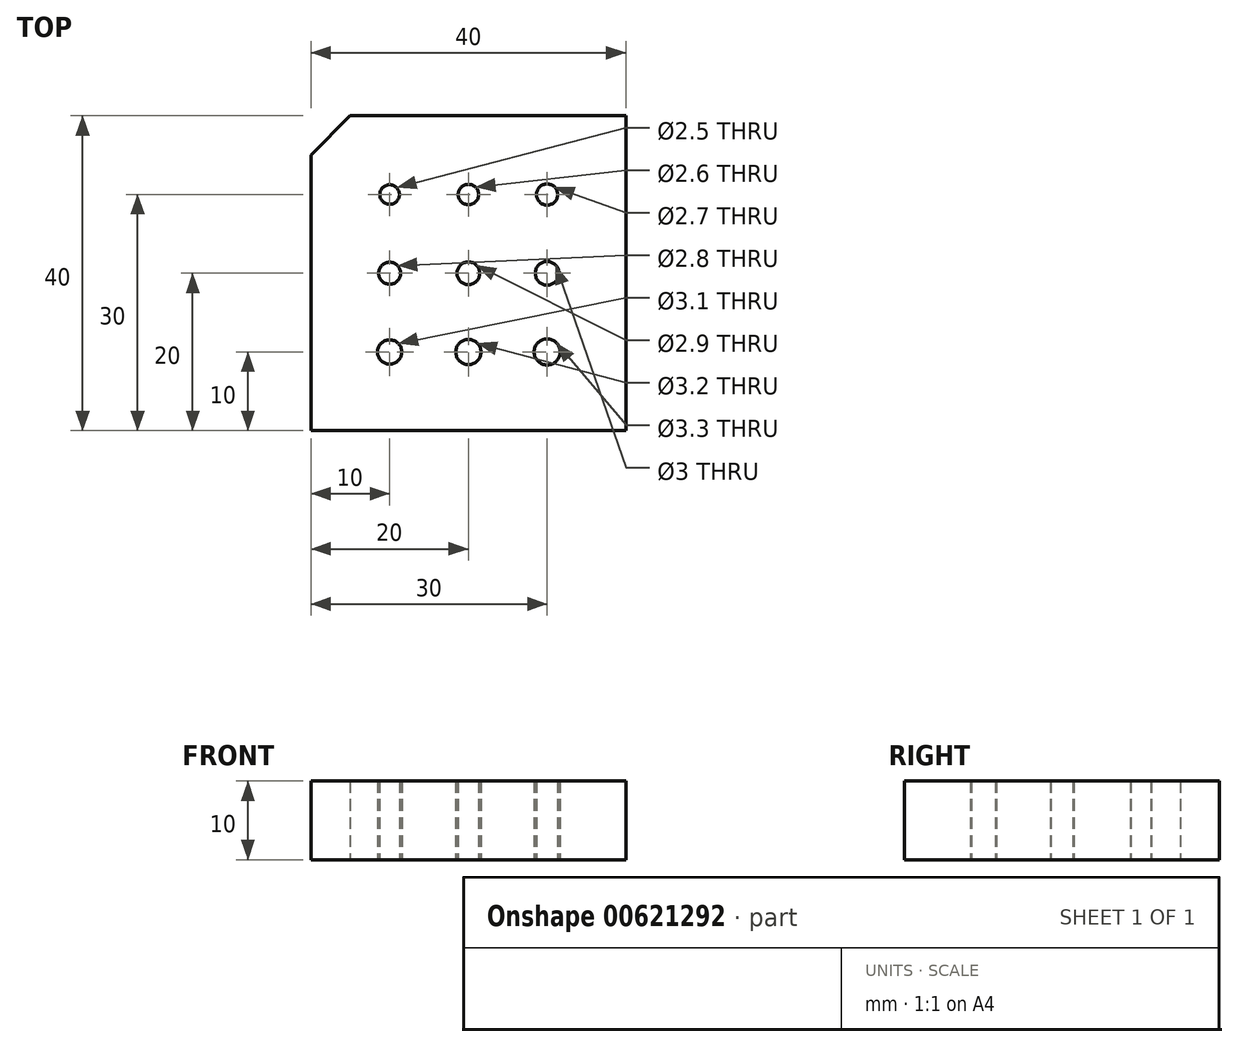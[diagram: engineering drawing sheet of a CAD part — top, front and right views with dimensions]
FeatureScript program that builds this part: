
annotation { "Feature Type Name" : "Feature", "Feature Type Description" : "" }
export const myFeature = defineFeature(function(context is Context, id is Id, definition is map)
    precondition{}
    {
        {
            var Q0;
            Q0=qCreatedBy(makeId("Top.planeOp"),FACE);
            var sketch = newSketch(context, id + "F0", { "sketchPlane" : qUnion([Q0])});
            skLineSegment(sketch, "E0.bottom", {"start": v(0, 0) * mm, "end": v(10, 0) * mm, "construction": true});
            skLineSegment(sketch, "E0.top", {"start": v(0, 10) * mm, "end": v(10, 10) * mm, "construction": true});
            skLineSegment(sketch, "E0.left", {"start": v(0, 0) * mm, "end": v(0, 10) * mm, "construction": true});
            skLineSegment(sketch, "E0.right", {"start": v(10, 0) * mm, "end": v(10, 10) * mm, "construction": true});
            skLineSegment(sketch, "E1.bottom", {"start": v(10, 0) * mm, "end": v(20, 0) * mm, "construction": true});
            skLineSegment(sketch, "E1.top", {"start": v(10, 10) * mm, "end": v(20, 10) * mm, "construction": true});
            skLineSegment(sketch, "E1.right", {"start": v(20, 0) * mm, "end": v(20, 10) * mm, "construction": true});
            skLineSegment(sketch, "E2.bottom", {"start": v(0, 0) * mm, "end": v(-10, 0) * mm, "construction": true});
            skLineSegment(sketch, "E2.top", {"start": v(0, 10) * mm, "end": v(-10, 10) * mm, "construction": true});
            skLineSegment(sketch, "E2.right", {"start": v(-10, 0) * mm, "end": v(-10, 10) * mm, "construction": true});
            skLineSegment(sketch, "E3.bottom", {"start": v(-10, 0) * mm, "end": v(-20, 0) * mm, "construction": true});
            skLineSegment(sketch, "E3.top", {"start": v(-10, 10) * mm, "end": v(-20, 10) * mm, "construction": true});
            skLineSegment(sketch, "E3.right", {"start": v(-20, 0) * mm, "end": v(-20, 10) * mm, "construction": true});
            skLineSegment(sketch, "E4.top", {"start": v(0, -10) * mm, "end": v(-10, -10) * mm, "construction": true});
            skLineSegment(sketch, "E4.left", {"start": v(0, 0) * mm, "end": v(0, -10) * mm, "construction": true});
            skLineSegment(sketch, "E4.right", {"start": v(-10, 0) * mm, "end": v(-10, -10) * mm, "construction": true});
            skLineSegment(sketch, "E5.bottom", {"start": v(-10, -10) * mm, "end": v(-20, -10) * mm, "construction": true});
            skLineSegment(sketch, "E5.left", {"start": v(-10, -10) * mm, "end": v(-10, 0) * mm, "construction": true});
            skLineSegment(sketch, "E5.right", {"start": v(-20, -10) * mm, "end": v(-20, 0) * mm, "construction": true});
            skLineSegment(sketch, "E6.top", {"start": v(0, -10) * mm, "end": v(10, -10) * mm, "construction": true});
            skLineSegment(sketch, "E6.right", {"start": v(10, 0) * mm, "end": v(10, -10) * mm, "construction": true});
            skLineSegment(sketch, "E7.bottom", {"start": v(10, -10) * mm, "end": v(20, -10) * mm, "construction": true});
            skLineSegment(sketch, "E7.left", {"start": v(10, -10) * mm, "end": v(10, 0) * mm, "construction": true});
            skLineSegment(sketch, "E7.right", {"start": v(20, -10) * mm, "end": v(20, 0) * mm, "construction": true});
            skLineSegment(sketch, "E8.bottom", {"start": v(20, 10) * mm, "end": v(10, 10) * mm, "construction": true});
            skLineSegment(sketch, "E8.top", {"start": v(20, 20) * mm, "end": v(10, 20) * mm, "construction": true});
            skLineSegment(sketch, "E8.left", {"start": v(20, 10) * mm, "end": v(20, 20) * mm, "construction": true});
            skLineSegment(sketch, "E8.right", {"start": v(10, 10) * mm, "end": v(10, 20) * mm, "construction": true});
            skLineSegment(sketch, "E9.top", {"start": v(0, 20) * mm, "end": v(10, 20) * mm, "construction": true});
            skLineSegment(sketch, "E9.left", {"start": v(0, 10) * mm, "end": v(0, 20) * mm, "construction": true});
            skLineSegment(sketch, "E10.bottom", {"start": v(0, 20) * mm, "end": v(-10, 20) * mm, "construction": true});
            skLineSegment(sketch, "E10.left", {"start": v(0, 20) * mm, "end": v(0, 10) * mm, "construction": true});
            skLineSegment(sketch, "E10.right", {"start": v(-10, 20) * mm, "end": v(-10, 10) * mm, "construction": true});
            skLineSegment(sketch, "E11.bottom", {"start": v(-10, 20) * mm, "end": v(-20, 20) * mm, "construction": true});
            skLineSegment(sketch, "E11.right", {"start": v(-20, 20) * mm, "end": v(-20, 10) * mm, "construction": true});
            skLineSegment(sketch, "E12.bottom", {"start": v(-20, -10) * mm, "end": v(-10, -10) * mm, "construction": true});
            skLineSegment(sketch, "E12.top", {"start": v(-20, -20) * mm, "end": v(-10, -20) * mm, "construction": true});
            skLineSegment(sketch, "E12.left", {"start": v(-20, -10) * mm, "end": v(-20, -20) * mm, "construction": true});
            skLineSegment(sketch, "E12.right", {"start": v(-10, -10) * mm, "end": v(-10, -20) * mm, "construction": true});
            skLineSegment(sketch, "E13.bottom", {"start": v(-10, -20) * mm, "end": v(0, -20) * mm, "construction": true});
            skLineSegment(sketch, "E13.top", {"start": v(-10, -10) * mm, "end": v(0, -10) * mm, "construction": true});
            skLineSegment(sketch, "E13.left", {"start": v(-10, -20) * mm, "end": v(-10, -10) * mm, "construction": true});
            skLineSegment(sketch, "E13.right", {"start": v(0, -20) * mm, "end": v(0, -10) * mm, "construction": true});
            skLineSegment(sketch, "E14.bottom", {"start": v(0, -20) * mm, "end": v(10, -20) * mm, "construction": true});
            skLineSegment(sketch, "E14.right", {"start": v(10, -20) * mm, "end": v(10, -10) * mm, "construction": true});
            skLineSegment(sketch, "E15.bottom", {"start": v(10, -20) * mm, "end": v(20, -20) * mm, "construction": true});
            skLineSegment(sketch, "E15.right", {"start": v(20, -20) * mm, "end": v(20, -10) * mm, "construction": true});
            skCircle(sketch, "E16", {"center": v(-10, 10) * mm, "radius": 1.25 * mm});
            skCircle(sketch, "E17", {"center": v(0, 10) * mm, "radius": 1.3 * mm});
            skCircle(sketch, "E18", {"center": v(10, 10) * mm, "radius": 1.35 * mm});
            skCircle(sketch, "E19", {"center": v(-10, 0) * mm, "radius": 1.4 * mm});
            skCircle(sketch, "E20", {"center": v(-10, -10) * mm, "radius": 1.55 * mm});
            skCircle(sketch, "E21", {"center": v(0, 0) * mm, "radius": 1.45 * mm});
            skCircle(sketch, "E22", {"center": v(0, -10) * mm, "radius": 1.6 * mm});
            skCircle(sketch, "E23", {"center": v(10, -10) * mm, "radius": 1.65 * mm});
            skCircle(sketch, "E24", {"center": v(10, 0) * mm, "radius": 1.5 * mm});
            skLineSegment(sketch, "E25", {"start": v(-20, 15) * mm, "end": v(-15, 20) * mm});
            skLineSegment(sketch, "E26", {"start": v(-15, 20) * mm, "end": v(20, 20) * mm});
            skLineSegment(sketch, "E27", {"start": v(20, -20) * mm, "end": v(-20, -20) * mm});
            skLineSegment(sketch, "E28", {"start": v(-20, 15) * mm, "end": v(-20, -20) * mm});
            skLineSegment(sketch, "E29", {"start": v(20, -20) * mm, "end": v(20, 20) * mm});
            skSolve(sketch);
        }
        {
            var Q0;
            Q0 = qSketchRegion(id + "F0", true);
            extrude(context, id + "F1", {"entities" : qUnion([Q0]), "depth" : 10 * mm, "offsetDistance" : 25 * mm});
        }
    });
